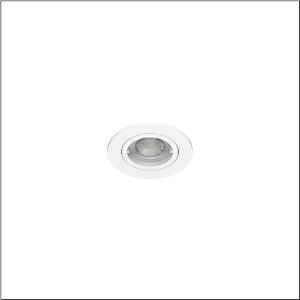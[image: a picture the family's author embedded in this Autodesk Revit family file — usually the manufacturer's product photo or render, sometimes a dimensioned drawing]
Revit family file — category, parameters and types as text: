
# Revit family: lunis_41_spot_51dt137a42a
name_source: partatom
category: Lighting Fixtures
units: mm (PartAtom-declared; Revit-internal decimal feet)

## family parameters
Cut with Voids When Loaded = No
Host = Face
Light Source = No
Part Type = Normal
Room Calculation Point = No
Round Connector Dimension = Use Diameter
Shared = No

## types (1)
- Lunis 41 Spot (1 x LED, 720 lm, 6.5 W, 4000K)
    Apparent Load = 7 VA
    CIE Flux Codes = 87 97 99 100 100
    Color Rendering = 80
    Color Temperature = 4000K
    Default Elevation = 1800 mm
    Description = Lunis 41,  Spot, downlight, light emission: direct distribution, LED rated luminous flux: 720lm, light colour: 840, control gear: ECG, mains connection: 230V, AC, 50/60Hz, housing, round, of aluminium, coated, traffic white (RAL 9016), diameter: 88mm, recess depth: 54mm, protection rating (complete): IP20, protection rating (on room side): IP20, insulation class (complete): insulation class II (safety insulation), certification: CE, permissible ambient temperature for indoor applications: -20..+40°C, packaging unit: 1 piece
    Height = 0 mm  [stored 0 ft]
    Lamp = 1 x LED
    Lamp Light Flux = 720 lm
    Lamp Power = 6.5 W
    Lamp count = 1
    Length = 88 mm
    Luminous efficacy = 111 lm/W
    Manufacturer = Siteco
    ModVariant = No
    Model = 51DT137A42A
    Mounting Place = Ceiling
    Mounting Type = Recessed
    Number of Poles = 1
    OnlyDefault = Yes
    Power Factor = 1
    Product Name = Lunis 41 Spot
    Product group = downlight
    ProductGroupID = 400
    Protection Class = Protection class II
    Protection Degree = IP 20
    RLX_Detail_Level = 1
    RLX_Emergency_Light_Flux = 0 lm
    RLX_Emergency_Type = 0
    RLX_Emergency_Type_DB = No
    RlxData = <blob elided: 37945 chars, md5=bcb84507>
    Socket = socket
    Standby Power = 0 W
    System Light Flux = 720 lm
    System Power = 7 W
    Type Comments = Product without accessories
    Type Image = l_1005286.jpg
    URL = http://relux.com
    VarID = ---
    Voltage = 0 V
    Weight = 0.00 kg
    Width = 0 mm  [stored 0 ft]

note: [stored X ft] marks values corroborated as IEEE doubles in the binary element streams (Revit-internal decimal feet)

## geometry (parser evidence)
native form markers: Blend x4, Sweep x10
no freeform markers — native parametric forms only
